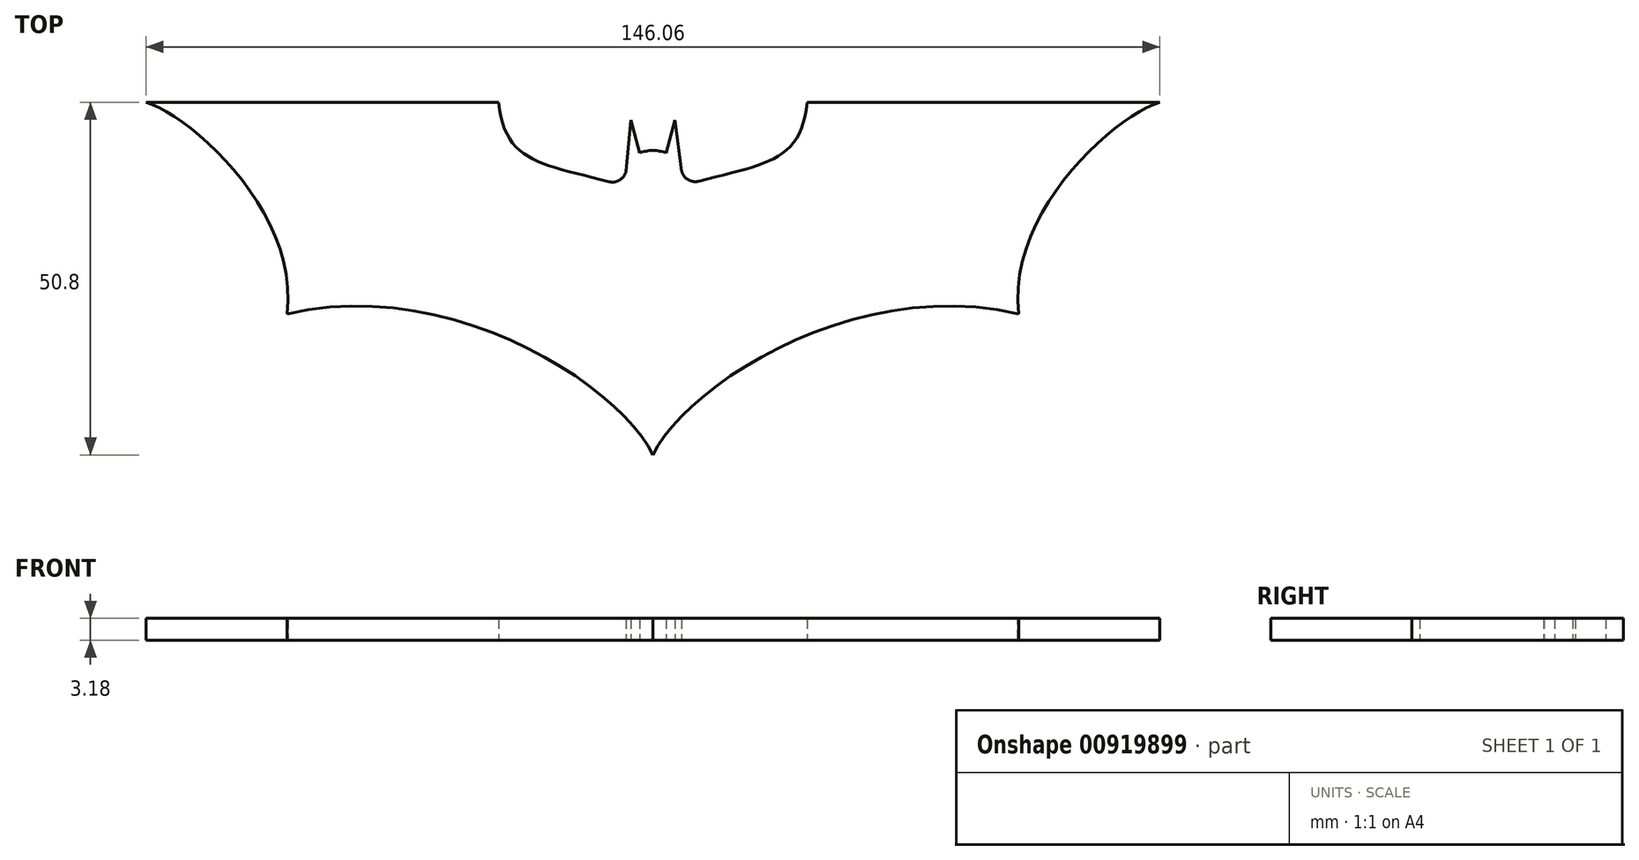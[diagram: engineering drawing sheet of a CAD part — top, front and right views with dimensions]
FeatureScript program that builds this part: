
annotation { "Feature Type Name" : "Feature", "Feature Type Description" : "" }
export const myFeature = defineFeature(function(context is Context, id is Id, definition is map)
    precondition{}
    {
        {
            var Q0;
            Q0=qCreatedBy(makeId("Top.planeOp"),FACE);
            var sketch = newSketch(context, id + "F0", { "sketchPlane" : qUnion([Q0])});
            skLineSegment(sketch, "E0", {"start": v(-73.03, 0) * mm, "end": v(-22.23, 0) * mm});
            skFitSpline(sketch, "E1", {"points": [v(-73.03, 0) * mm, v(-52.7, -30.48) * mm], "startDerivative": vector(19.44, -5.95) * mm, "endDerivative": vector(-5.24, -44.2) * mm});
            skFitSpline(sketch, "E2", {"points": [v(-52.7, -30.48) * mm, v(0, -50.8) * mm], "startDerivative": vector(70.99, 16.7) * mm, "endDerivative": vector(14.25, -29.82) * mm});
            skFitSpline(sketch, "E3", {"points": [v(-22.23, 0) * mm, v(-4.32, -11.98) * mm], "startDerivative": vector(2.79, -27.61) * mm, "endDerivative": vector(33.54, -9.48) * mm});
            skFitSpline(sketch, "E4.MirrorCS", {"points": [v(22.23, 0) * mm, v(4.32, -11.98) * mm], "startDerivative": vector(-2.79, -27.61) * mm, "endDerivative": vector(-33.54, -9.48) * mm});
            skLineSegment(sketch, "E5.MirrorCS", {"start": v(73.03, 0) * mm, "end": v(22.23, 0) * mm});
            skFitSpline(sketch, "E6.MirrorCS", {"points": [v(73.03, 0) * mm, v(52.7, -30.48) * mm], "startDerivative": vector(-19.44, -5.95) * mm, "endDerivative": vector(5.24, -44.2) * mm});
            skFitSpline(sketch, "E7.MirrorCS", {"points": [v(52.7, -30.48) * mm, v(0, -50.8) * mm], "startDerivative": vector(-70.99, 16.7) * mm, "endDerivative": vector(-14.25, -29.82) * mm});
            skLineSegment(sketch, "E8", {"start": v(-52.7, -30.48) * mm, "end": v(-50.34, -10.55) * mm, "construction": true});
            skLineSegment(sketch, "E9", {"start": v(-52.7, -30.48) * mm, "end": v(-31, -25.38) * mm, "construction": true});
            skArc(sketch, "E10.filletArc", {"start": v(-6.34, -11.43) * mm, "mid": v(-4.79, -11.2) * mm, "end": v(-3.88, -9.92) * mm});
            skArc(sketch, "E11.filletArc", {"start": v(4.14, -9.9) * mm, "mid": v(5.06, -11.15) * mm, "end": v(6.6, -11.36) * mm});
            skLineSegment(sketch, "E12.bottom", {"start": v(-22.23, 0) * mm, "end": v(-52.7, 0) * mm, "construction": true});
            skLineSegment(sketch, "E12.top", {"start": v(-22.23, -30.48) * mm, "end": v(-52.7, -30.48) * mm, "construction": true});
            skLineSegment(sketch, "E12.left", {"start": v(-22.23, 0) * mm, "end": v(-22.23, -30.48) * mm, "construction": true});
            skLineSegment(sketch, "E12.right", {"start": v(-52.7, 0) * mm, "end": v(-52.7, -30.48) * mm, "construction": true});
            skLineSegment(sketch, "E13", {"start": v(-22.23, -9.2) * mm, "end": v(-22.23, 0) * mm});
            skLineSegment(sketch, "E14", {"start": v(-3.88, -9.92) * mm, "end": v(-3.14, -2.54) * mm});
            skLineSegment(sketch, "E15", {"start": v(-3.14, -2.54) * mm, "end": v(-1.93, -7.3) * mm});
            skLineSegment(sketch, "E16", {"start": v(4.14, -9.9) * mm, "end": v(3.2, -2.54) * mm});
            skLineSegment(sketch, "E17", {"start": v(3.2, -2.54) * mm, "end": v(1.93, -7.3) * mm});
            skArc(sketch, "E18", {"start": v(1.93, -7.3) * mm, "mid": v(0, -6.94) * mm, "end": v(-1.93, -7.3) * mm});
            skSolve(sketch);
        }
        {
            var Q0;
            Q0=makeQuery(id+"F0.imprint","IMPRINT",FACE,{"disambiguationData":[TD([[makeQuery(id+"F0.imprint","IMPRINT",EDGE,{"derivedFrom":sQuery(id+"F0.wireOp",EDGE,"E0")}),-1.0]])]});
            extrude(context, id + "F1", {"entities" : qUnion([Q0]), "offsetDistance" : 25.4 * mm, "depth" : 3.17 * mm});
        }
    });
